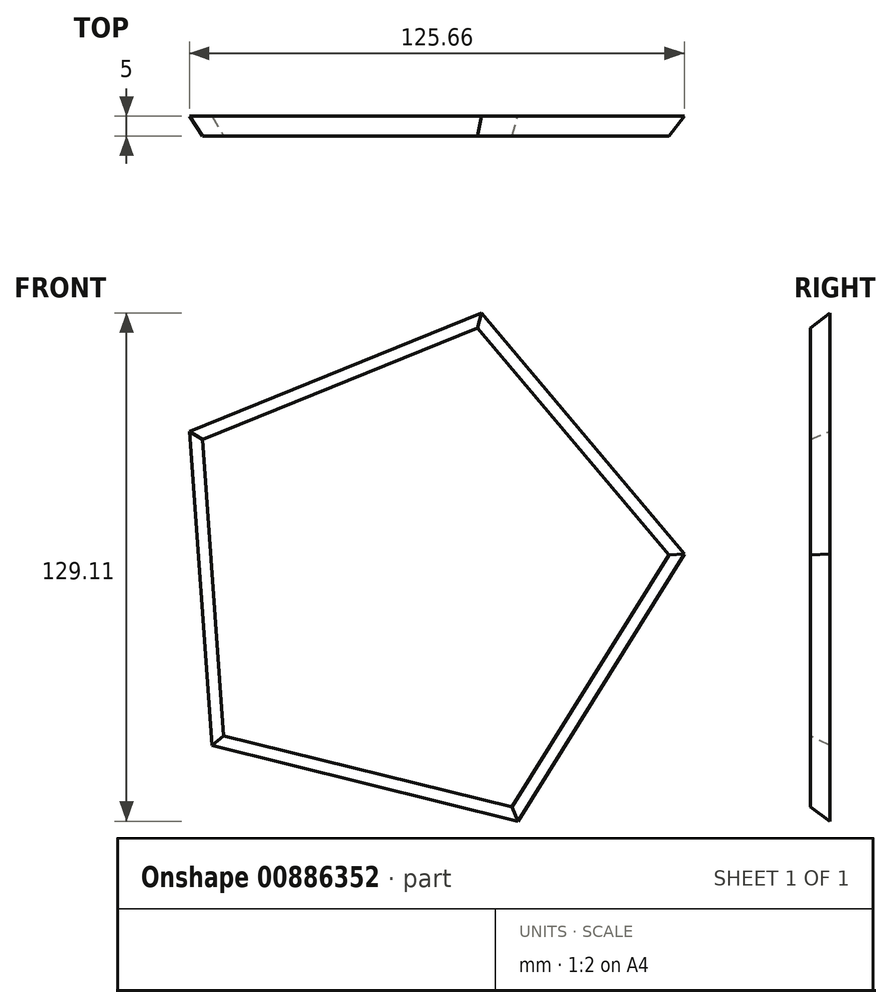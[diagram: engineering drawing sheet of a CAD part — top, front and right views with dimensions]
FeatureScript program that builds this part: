
annotation { "Feature Type Name" : "Feature", "Feature Type Description" : "" }
export const myFeature = defineFeature(function(context is Context, id is Id, definition is map)
    precondition{}
    {
        {
            var Q0;
            Q0=qCreatedBy(makeId("Front.planeOp"),FACE);
            var sketch = newSketch(context, id + "F0", { "sketchPlane" : qUnion([Q0])});
            skCircle(sketch, "E0.cCircle", {"center": v(0, 0) * mm, "radius": 55.06 * mm, "construction": true});
            skLineSegment(sketch, "E0.0", {"start": v(-52.05, -43.84) * mm, "end": v(-57.78, 35.95) * mm});
            skLineSegment(sketch, "E0.1", {"start": v(-57.78, 35.95) * mm, "end": v(16.34, 66.06) * mm});
            skLineSegment(sketch, "E0.2", {"start": v(16.34, 66.06) * mm, "end": v(67.88, 4.88) * mm});
            skLineSegment(sketch, "E0.3", {"start": v(67.88, 4.88) * mm, "end": v(25.61, -63.05) * mm});
            skLineSegment(sketch, "E0.4", {"start": v(25.61, -63.05) * mm, "end": v(-52.05, -43.84) * mm});
            skPoint(sketch, "E0.0.midPoint", {"position": v(-54.91, -3.95) * mm});
            skSolve(sketch);
        }
        {
            var Q0;
            Q0=makeQuery(id+"F0.imprint","IMPRINT",FACE,{"disambiguationData":[TD([[makeQuery(id+"F0.imprint","IMPRINT",EDGE,{"derivedFrom":sQuery(id+"F0.wireOp",EDGE,"E0.0")}),-1.0]])]});
            extrude(context, id + "F1", {"entities" : qUnion([Q0]), "depth" : 5 * mm, "offsetDistance" : 25 * mm});
        }
        {
            var Q0;
            Q0=makeQuery(id+"F1.opExtrude","CAP_EDGE",EDGE,{"disambiguationData":[OSD([sQuery(id+"F0.wireOp",EDGE,"E0.0")])],"isStart":false});
            var Q1;
            Q1=makeQuery(id+"F1.opExtrude","CAP_EDGE",EDGE,{"disambiguationData":[OSD([sQuery(id+"F0.wireOp",EDGE,"E0.1")])],"isStart":false});
            var Q2;
            Q2=makeQuery(id+"F1.opExtrude","CAP_EDGE",EDGE,{"disambiguationData":[OSD([sQuery(id+"F0.wireOp",EDGE,"E0.2")])],"isStart":false});
            var Q3;
            Q3=makeQuery(id+"F1.opExtrude","CAP_EDGE",EDGE,{"disambiguationData":[OSD([sQuery(id+"F0.wireOp",EDGE,"E0.3")])],"isStart":false});
            var Q4;
            Q4=makeQuery(id+"F1.opExtrude","CAP_EDGE",EDGE,{"disambiguationData":[OSD([sQuery(id+"F0.wireOp",EDGE,"E0.4")])],"isStart":false});
            chamfer(context, id + "F2", {"entities" : qUnion([Q0, Q1, Q2, Q3, Q4]), "chamferType" : ChamferType.OFFSET_ANGLE, "width" : 5 * mm, "oppositeDirection" : false, "angle" : 32 * degree, "tangentPropagation" : true});
        }
    });
